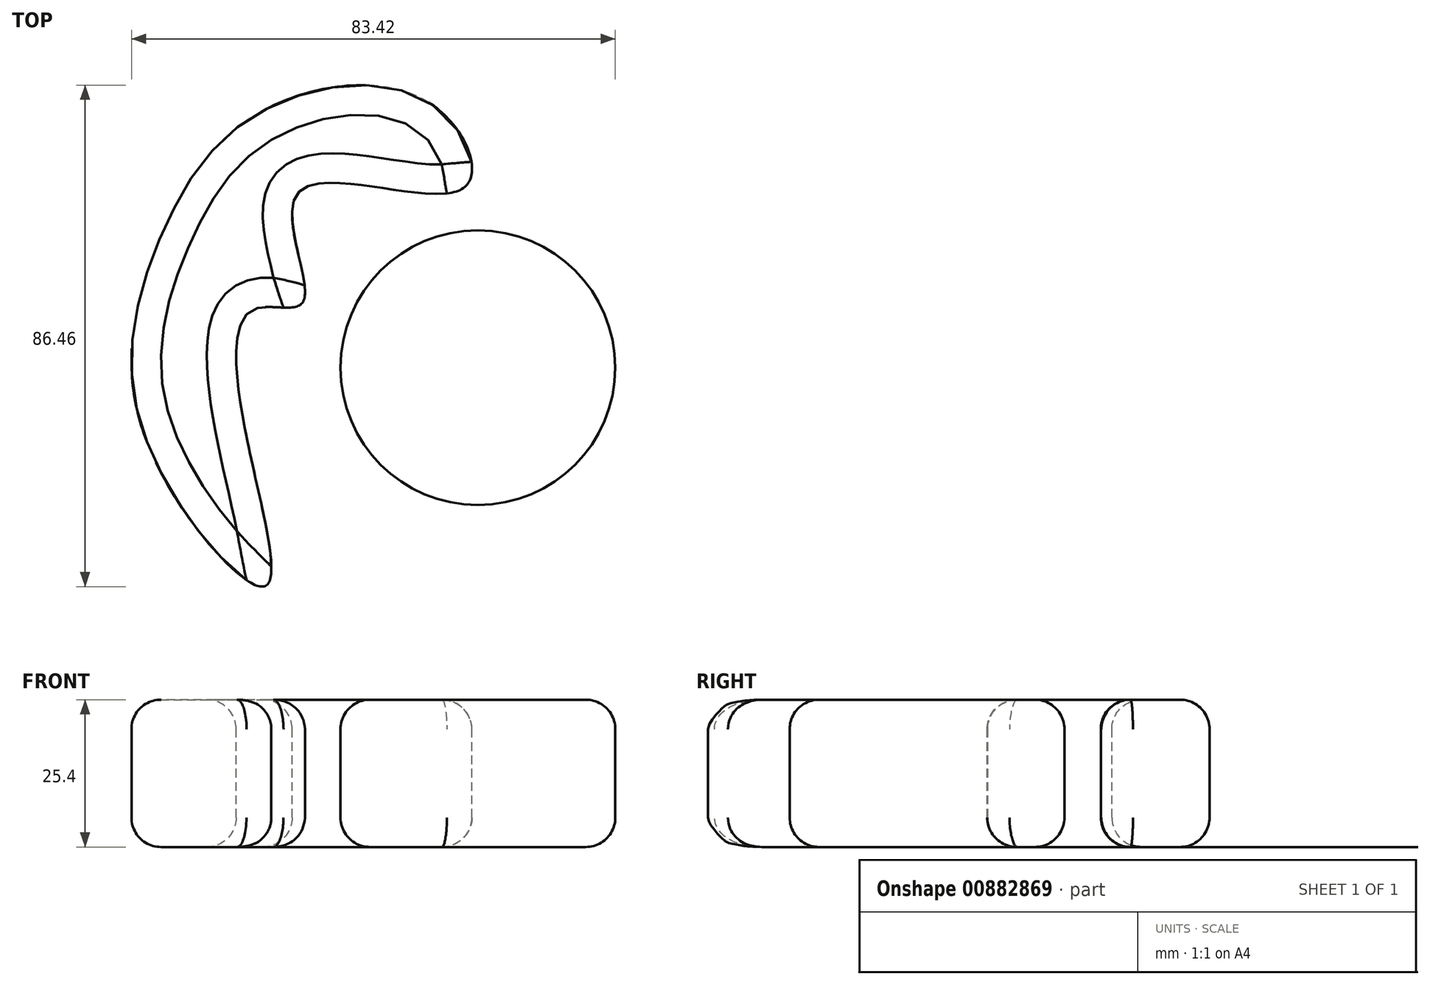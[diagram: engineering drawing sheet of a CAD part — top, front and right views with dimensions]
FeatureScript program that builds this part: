
annotation { "Feature Type Name" : "Feature", "Feature Type Description" : "" }
export const myFeature = defineFeature(function(context is Context, id is Id, definition is map)
    precondition{}
    {
        {
            var Q0;
            Q0=qCreatedBy(makeId("Top.planeOp"),FACE);
            var sketch = newSketch(context, id + "F0", { "sketchPlane" : qUnion([Q0])});
            skCircle(sketch, "E0", {"center": v(0, 2.65) * mm, "radius": 23.69 * mm});
            skFitSpline(sketch, "E1", {"points": [v(-39.94, -9.03) * mm, v(-38.61, 12.74) * mm, v(-30.12, 14.06) * mm, v(-30.92, 32.9) * mm, v(-2.79, 33.43) * mm, v(-7.56, 47.76) * mm, v(-37.55, 46.7) * mm, v(-54.8, 24.94) * mm, v(-57.19, -9.82) * mm, v(-36.75, -35.03) * mm, v(-39.94, -9.03) * mm]});
            skSolve(sketch);
        }
        {
            var Q0;
            Q0 = qSketchRegion(id + "F0", true);
            extrude(context, id + "F1", {"entities" : qUnion([Q0]), "depth" : 25.4 * mm, "offsetDistance" : 25.4 * mm});
        }
        {
            var Q0;
            Q0=makeQuery(id+"F1.opExtrude","CAP_FACE",FACE,{"disambiguationData":[OSD([sQuery(id+"F0.wireOp",EDGE,"E0")])],"isStart":false});
            var Q1;
            Q1=makeQuery(id+"F1.opExtrude","CAP_EDGE",EDGE,{"disambiguationData":[OSD([sQuery(id+"F0.wireOp",EDGE,"E0")])],"isStart":true});
            var Q2;
            Q2=makeQuery(id+"F1.opExtrude","SWEPT_FACE",FACE,{"disambiguationData":[OSD([sQuery(id+"F0.wireOp",EDGE,"E0")])]});
            var Q3;
            Q3=makeQuery(id+"F1.opExtrude","CAP_EDGE",EDGE,{"disambiguationData":[OSD([sQuery(id+"F0.wireOp",EDGE,"E1")])],"isStart":false});
            var Q4;
            Q4=makeQuery(id+"F1.opExtrude","CAP_EDGE",EDGE,{"disambiguationData":[OSD([sQuery(id+"F0.wireOp",EDGE,"E1")])],"isStart":true});
            fillet(context, id + "F2", {"entities" : qUnion([Q0, Q1, Q2, Q3, Q4]), "radius" : 5.08 * mm, "tangentPropagation" : true, "allowEdgeOverflow" : false});
        }
    });
